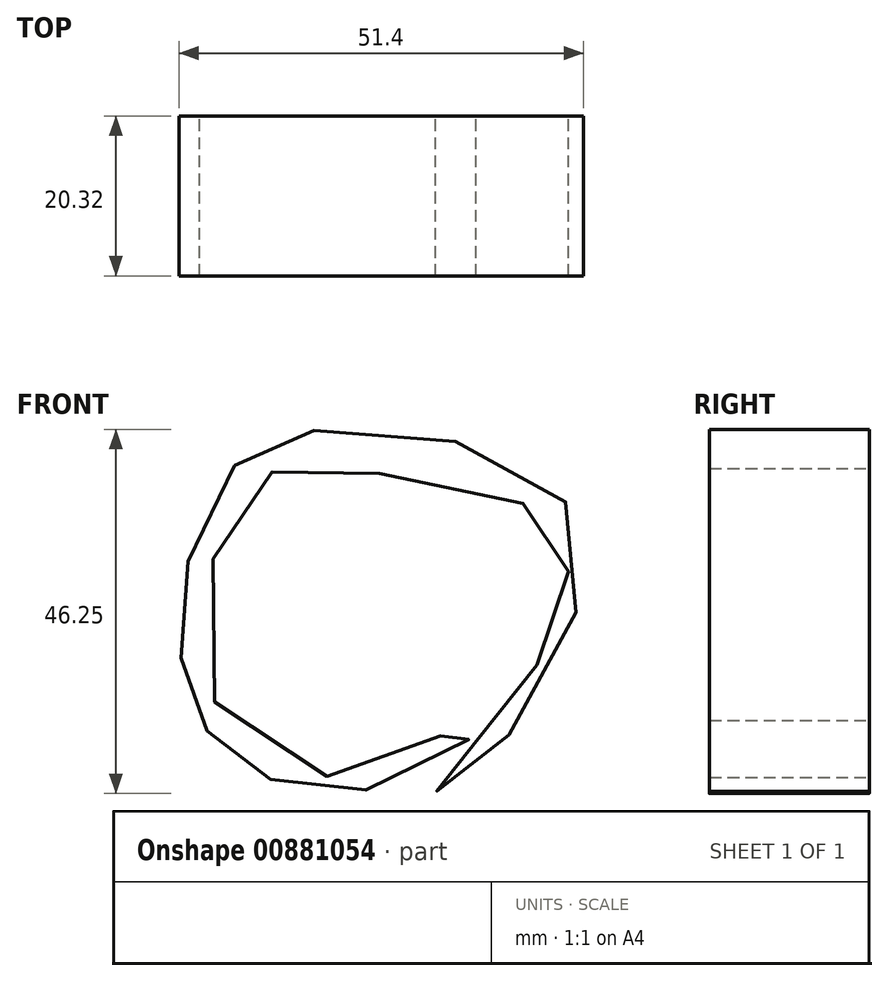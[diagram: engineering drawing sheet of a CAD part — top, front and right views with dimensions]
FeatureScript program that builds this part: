
annotation { "Feature Type Name" : "Feature", "Feature Type Description" : "" }
export const myFeature = defineFeature(function(context is Context, id is Id, definition is map)
    precondition{}
    {
        {
            var Q0;
            Q0=qCreatedBy(makeId("Front.planeOp"),FACE);
            var sketch = newSketch(context, id + "F0", { "sketchPlane" : qUnion([Q0])});
            skFitSpline(sketch, "E0", {"points": [v(0, 21.64) * mm, v(27.43, 16.76) * mm, v(34.1, 2.55) * mm, v(21.88, -20.1) * mm, v(15.44, -24.1) * mm, v(19.66, -18.77) * mm, v(27.65, -9.22) * mm, v(32.31, 3.88) * mm, v(27.65, 11.87) * mm, v(0, 16.76) * mm, v(-8.1, 14.31) * mm, v(-13.64, -10.55) * mm, v(6.56, -22.1) * mm, v(19.66, -15.21) * mm, v(20.55, -16.32) * mm, v(7.23, -23.87) * mm, v(-5.87, -22.54) * mm, v(-13.2, -17) * mm, v(-16.53, -9.44) * mm, v(-16.53, 2.77) * mm, v(-9.87, 17.42) * mm, v(0, 21.64) * mm]});
            skSolve(sketch);
        }
        {
            var Q0;
            Q0=makeQuery(id+"F0.imprint","IMPRINT",FACE,{"disambiguationData":[TD([[makeQuery(id+"F0.imprint","IMPRINT",EDGE,{"derivedFrom":sQuery(id+"F0.wireOp",EDGE,"E0")}),-1.0]])]});
            extrude(context, id + "F1", {"entities" : qUnion([Q0]), "depth" : 20.32 * mm, "offsetDistance" : 25.4 * mm});
        }
    });
